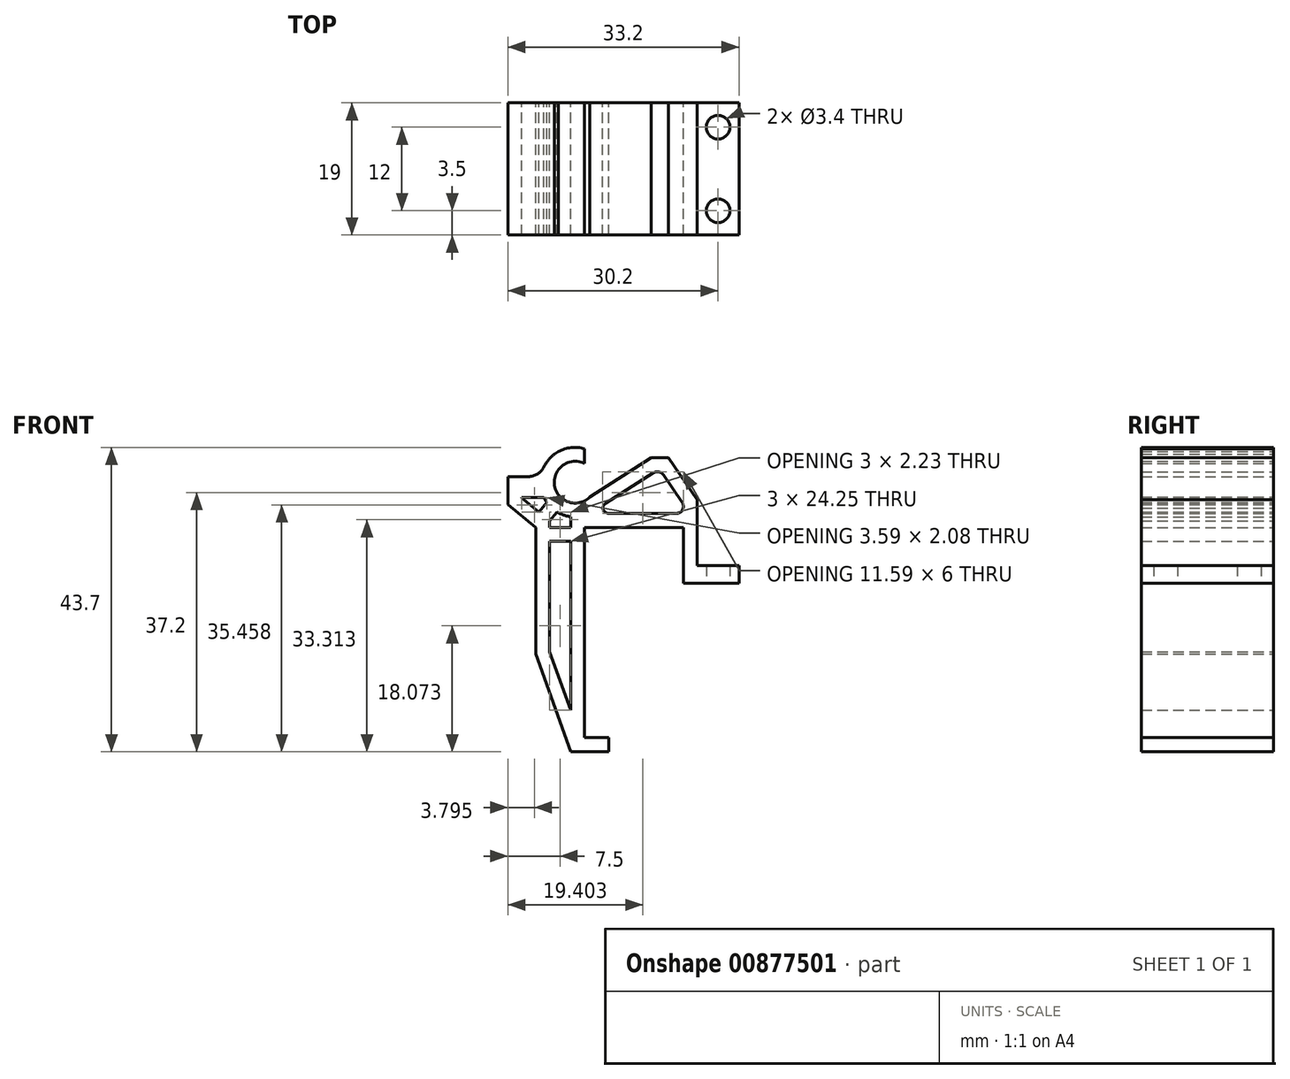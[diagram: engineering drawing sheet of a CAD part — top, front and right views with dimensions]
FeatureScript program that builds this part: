
annotation { "Feature Type Name" : "Feature", "Feature Type Description" : "" }
export const myFeature = defineFeature(function(context is Context, id is Id, definition is map)
    precondition{}
    {
        {
            var Q0;
            Q0=qCreatedBy(makeId("Front.planeOp"),FACE);
            var sketch = newSketch(context, id + "F0", { "sketchPlane" : qUnion([Q0])});
            skLineSegment(sketch, "E0", {"start": v(0, 0) * mm, "end": v(-5.5, 0) * mm});
            skLineSegment(sketch, "E1", {"start": v(0, 0) * mm, "end": v(0, 2) * mm});
            skLineSegment(sketch, "E2", {"start": v(0, 2) * mm, "end": v(-3.5, 2) * mm});
            skLineSegment(sketch, "E3", {"start": v(-3.5, 2) * mm, "end": v(-3.5, 32.2) * mm});
            skLineSegment(sketch, "E4", {"start": v(-3.5, 32.2) * mm, "end": v(10.7, 32.2) * mm});
            skLineSegment(sketch, "E5", {"start": v(10.7, 32.2) * mm, "end": v(10.7, 24.2) * mm});
            skLineSegment(sketch, "E6", {"start": v(10.7, 24.2) * mm, "end": v(18.7, 24.2) * mm});
            skLineSegment(sketch, "E7", {"start": v(18.7, 24.2) * mm, "end": v(18.7, 26.7) * mm});
            skLineSegment(sketch, "E8", {"start": v(18.7, 26.7) * mm, "end": v(12.7, 26.7) * mm});
            skLineSegment(sketch, "E9", {"start": v(12.7, 26.7) * mm, "end": v(12.7, 36.2) * mm});
            skLineSegment(sketch, "E10.0", {"start": v(-0.91, 34.2) * mm, "end": v(10.7, 34.2) * mm});
            skLineSegment(sketch, "E11.0", {"start": v(-10.5, 14) * mm, "end": v(-10.5, 32.2) * mm});
            skLineSegment(sketch, "E12", {"start": v(-10.5, 14) * mm, "end": v(-5.5, 0) * mm});
            skLineSegment(sketch, "E13.0", {"start": v(-8.5, 14.35) * mm, "end": v(-5.5, 5.95) * mm});
            skLineSegment(sketch, "E14.trimOffspring", {"start": v(-8.5, 14.35) * mm, "end": v(-8.5, 30.2) * mm});
            skLineSegment(sketch, "E15", {"start": v(-8.5, 32.2) * mm, "end": v(-5.5, 32.2) * mm});
            skLineSegment(sketch, "E16", {"start": v(-5.5, 30.2) * mm, "end": v(-5.5, 5.95) * mm});
            skLineSegment(sketch, "E17", {"start": v(-3.5, 32.2) * mm, "end": v(6, 32.2) * mm});
            skLineSegment(sketch, "E18", {"start": v(12.7, 36.2) * mm, "end": v(8.59, 42.2) * mm});
            skLineSegment(sketch, "E19.0", {"start": v(10.7, 35.58) * mm, "end": v(7.53, 40.2) * mm});
            skLineSegment(sketch, "E20", {"start": v(11.52, 34.2) * mm, "end": v(11.52, 34.39) * mm});
            skLineSegment(sketch, "E21", {"start": v(-5.5, 0) * mm, "end": v(-5.5, 30.2) * mm});
            skLineSegment(sketch, "E22.0", {"start": v(-14.5, 14) * mm, "end": v(-14.5, 35.5) * mm});
            skLineSegment(sketch, "E23", {"start": v(-10.5, 32.2) * mm, "end": v(-14.5, 35.5) * mm});
            skLineSegment(sketch, "E24", {"start": v(-14.5, 35.5) * mm, "end": v(-14.5, 39.5) * mm});
            skLineSegment(sketch, "E25", {"start": v(-14.5, 39.5) * mm, "end": v(-11.58, 39.5) * mm});
            skLineSegment(sketch, "E26.0", {"start": v(-19.5, 35.5) * mm, "end": v(-19.5, 39.5) * mm});
            skLineSegment(sketch, "E27.0", {"start": v(-12.5, 36.44) * mm, "end": v(-12.5, 36.5) * mm});
            skLineSegment(sketch, "E28", {"start": v(8.59, 42.2) * mm, "end": v(6.09, 42.2) * mm});
            skLineSegment(sketch, "E29.0", {"start": v(7.53, 40.2) * mm, "end": v(6.67, 40.2) * mm});
            skLineSegment(sketch, "E30.trimOffspring", {"start": v(-10.77, 35.02) * mm, "end": v(-12.5, 36.44) * mm});
            skLineSegment(sketch, "E31.trimOffspring", {"start": v(-8.5, 32.2) * mm, "end": v(-8.5, 33.14) * mm});
            skLineSegment(sketch, "E32.trimOffspring", {"start": v(-5.5, 32.2) * mm, "end": v(-5.5, 33.74) * mm});
            skLineSegment(sketch, "E33", {"start": v(-13.88, 0) * mm, "end": v(-4.33, 0) * mm});
            skLineSegment(sketch, "E34.0", {"start": v(-12.5, 36.5) * mm, "end": v(-9.34, 36.5) * mm});
            skLineSegment(sketch, "E35", {"start": v(6.09, 42.2) * mm, "end": v(-2.85, 36.5) * mm});
            skLineSegment(sketch, "E36.0", {"start": v(6.67, 40.2) * mm, "end": v(-0.91, 35.36) * mm});
            skLineSegment(sketch, "E37", {"start": v(-0.91, 34.2) * mm, "end": v(-0.91, 35.36) * mm});
            skArc(sketch, "E38", {"start": v(-6.66, 41.09) * mm, "mid": v(-7.1, 36.73) * mm, "end": v(-2.73, 36.58) * mm});
            skPoint(sketch, "E39.orphan", {"position": v(-10.5, 39.5) * mm});
            skArc(sketch, "E40.0", {"start": v(-9.67, 40.02) * mm, "mid": v(-9.73, 39.75) * mm, "end": v(-9.78, 39.49) * mm});
            skArc(sketch, "E41.trimOffspring", {"start": v(-9.34, 36.5) * mm, "mid": v(-5.68, 33.77) * mm, "end": v(-1.33, 35.15) * mm});
            skPoint(sketch, "E42.orphan", {"position": v(-6.89, 36.5) * mm});
            skLineSegment(sketch, "E43.trimOffspring", {"start": v(-2.9, 36.42) * mm, "end": v(-2.85, 36.5) * mm});
            skLineSegment(sketch, "E44", {"start": v(-0.91, 35.36) * mm, "end": v(-1.33, 35.15) * mm});
            skLineSegment(sketch, "E45", {"start": v(-8.5, 33.14) * mm, "end": v(-7.44, 34.43) * mm});
            skLineSegment(sketch, "E46", {"start": v(-10.04, 34.42) * mm, "end": v(-8.91, 35.79) * mm});
            skPoint(sketch, "E47.orphan", {"position": v(-8.32, 36.5) * mm});
            skPoint(sketch, "E48.orphan", {"position": v(-6.95, 35.02) * mm});
            skLineSegment(sketch, "E49", {"start": v(-10.04, 34.42) * mm, "end": v(-10.77, 35.02) * mm});
            skLineSegment(sketch, "E50.trimOffspring", {"start": v(6, 42.14) * mm, "end": v(6, 42.44) * mm});
            skArc(sketch, "E51.0", {"start": v(-7.8, 42.73) * mm, "mid": v(-8.68, 41.9) * mm, "end": v(-9.34, 40.9) * mm});
            skLineSegment(sketch, "E51.1", {"start": v(-7.26, 43.08) * mm, "end": v(-7.8, 42.73) * mm});
            skLineSegment(sketch, "E52", {"start": v(10.7, 34.2) * mm, "end": v(10.7, 35.58) * mm});
            skArc(sketch, "E53.filletArc", {"start": v(-11.58, 39.5) * mm, "mid": v(-10.26, 39.88) * mm, "end": v(-9.34, 40.9) * mm});
            skArc(sketch, "E54", {"start": v(-3.5, 41.38) * mm, "mid": v(-7.8, 38.22) * mm, "end": v(-2.73, 36.58) * mm});
            skArc(sketch, "E55", {"start": v(-3.5, 43.52) * mm, "mid": v(-9.69, 37.44) * mm, "end": v(-1.33, 35.15) * mm});
            skLineSegment(sketch, "E56.trimOffspring", {"start": v(-6.24, 41.35) * mm, "end": v(-6.66, 41.09) * mm});
            skLineSegment(sketch, "E57.trimOffspring", {"start": v(-3.5, 41.38) * mm, "end": v(-3.5, 43.52) * mm});
            skLineSegment(sketch, "E58", {"start": v(-8.5, 30.2) * mm, "end": v(-8.5, 32.2) * mm});
            skLineSegment(sketch, "E59", {"start": v(-5.5, 30.2) * mm, "end": v(-5.5, 32.39) * mm});
            skLineSegment(sketch, "E60", {"start": v(-8.5, 33.14) * mm, "end": v(-10.04, 34.42) * mm});
            skLineSegment(sketch, "E61", {"start": v(-8.5, 30.2) * mm, "end": v(-5.5, 30.2) * mm});
            skSolve(sketch);
        }
        {
            var Q0;
            {var subQ0=sQuery(id+"F0.wireOp",EDGE,"E15");Q0=makeQuery(id+"F0.imprint","IMPRINT",FACE,{"disambiguationData":[TD([[makeQuery(id+"F0.imprint","IMPRINT",EDGE,{"derivedFrom":subQ0}),-1.0]])]});}
            var Q1;
            {var subQ0=sQuery(id+"F0.wireOp",EDGE,"E45");Q1=makeQuery(id+"F0.imprint","IMPRINT",FACE,{"disambiguationData":[TD([[makeQuery(id+"F0.imprint","IMPRINT",EDGE,{"derivedFrom":subQ0}),1.0]])]});}
            var Q2;
            Q2=makeQuery(id+"F0.imprint","IMPRINT",FACE,{"disambiguationData":[TD([[makeQuery(id+"F0.imprint","IMPRINT",EDGE,{"derivedFrom":sQuery(id+"F0.wireOp",EDGE,"E11.0")}),-1.0]])]});
            var Q3;
            {var subQ15=sQuery(id+"F0.wireOp",EDGE,"E0");Q3=makeQuery(id+"F0.imprint","IMPRINT",FACE,{"disambiguationData":[TD([[makeQuery(id+"F0.imprint","IMPRINT",EDGE,{"derivedFrom":subQ15}),-1.0]])]});}
            extrude(context, id + "F1", {"entities" : qUnion([Q0, Q1, Q2, Q3]), "depth" : 19 * mm, "offsetDistance" : 25 * mm});
        }
        {
            var Q0;
            Q0=makeQuery(id+"F1.opExtrude","SWEPT_FACE",FACE,{"disambiguationData":[OSD([sQuery(id+"F0.wireOp",EDGE,"E8")])]});
            var sketch = newSketch(context, id + "F2", { "sketchPlane" : qUnion([Q0])});
            skLineSegment(sketch, "E62", {"start": v(15.7, -19) * mm, "end": v(15.7, 0) * mm});
            skLineSegment(sketch, "E63", {"start": v(15.7, -9.5) * mm, "end": v(15.7, -15.5) * mm});
            skLineSegment(sketch, "E64", {"start": v(15.7, -15.5) * mm, "end": v(15.7, -3.5) * mm});
            skSolve(sketch);
        }
        {
            var Q0;
            Q0=sQuery(id+"F2.wireOp",VERTEX,"E63.end");
            var Q1;
            Q1=sQuery(id+"F2.wireOp",VERTEX,"E64.end");
            var Q2;
            Q2=makeQuery(id+"F1.opExtrude","SWEPT_BODY",BODY,{"disambiguationData":[OSD([sQuery(id+"F0.wireOp",EDGE,"E0"),sQuery(id+"F0.wireOp",EDGE,"E1"),sQuery(id+"F0.wireOp",EDGE,"E2"),sQuery(id+"F0.wireOp",EDGE,"E3"),sQuery(id+"F0.wireOp",EDGE,"E4"),sQuery(id+"F0.wireOp",EDGE,"E5"),sQuery(id+"F0.wireOp",EDGE,"E6"),sQuery(id+"F0.wireOp",EDGE,"E7"),sQuery(id+"F0.wireOp",EDGE,"E8"),sQuery(id+"F0.wireOp",EDGE,"E9"),sQuery(id+"F0.wireOp",EDGE,"E10.0"),sQuery(id+"F0.wireOp",EDGE,"E11.0"),sQuery(id+"F0.wireOp",EDGE,"E12"),sQuery(id+"F0.wireOp",EDGE,"E13.0"),sQuery(id+"F0.wireOp",EDGE,"E14.trimOffspring"),sQuery(id+"F0.wireOp",EDGE,"E17"),sQuery(id+"F0.wireOp",EDGE,"E18"),sQuery(id+"F0.wireOp",EDGE,"E19.0"),sQuery(id+"F0.wireOp",EDGE,"E21"),sQuery(id+"F0.wireOp",EDGE,"E23"),sQuery(id+"F0.wireOp",EDGE,"E24"),sQuery(id+"F0.wireOp",EDGE,"E25"),sQuery(id+"F0.wireOp",EDGE,"E27.0"),sQuery(id+"F0.wireOp",EDGE,"E28"),sQuery(id+"F0.wireOp",EDGE,"E29.0"),sQuery(id+"F0.wireOp",EDGE,"E30.trimOffspring"),sQuery(id+"F0.wireOp",EDGE,"E33"),sQuery(id+"F0.wireOp",EDGE,"E34.0"),sQuery(id+"F0.wireOp",EDGE,"E35"),sQuery(id+"F0.wireOp",EDGE,"E36.0"),sQuery(id+"F0.wireOp",EDGE,"E37"),sQuery(id+"F0.wireOp",EDGE,"E38"),sQuery(id+"F0.wireOp",EDGE,"E41.trimOffspring"),sQuery(id+"F0.wireOp",EDGE,"E45"),sQuery(id+"F0.wireOp",EDGE,"xdzNrTBE-XzyX-zclI-OnCp-i4VAQ6aGnxey"),sQuery(id+"F0.wireOp",EDGE,"E49"),sQuery(id+"F0.wireOp",EDGE,"7aTHKKxO-Tvbm-gAxb-JWcQ-REEeTTHWHdVK"),sQuery(id+"F0.wireOp",EDGE,"faeb26e9-fd7f-4cee-b89a-338b25216712.0"),sQuery(id+"F0.wireOp",EDGE,"E51.0"),sQuery(id+"F0.wireOp",EDGE,"E51.1"),sQuery(id+"F0.wireOp",EDGE,"t1PeDV6i-6xjs-lc1O-n51G-zDklkPdjoq5l"),sQuery(id+"F0.wireOp",EDGE,"E52"),sQuery(id+"F0.wireOp",EDGE,"E53.filletArc")])]});
            hole(context, id + "F3", {"style" : HoleStyle.SIMPLE, "endStyle" : HoleEndStyle.THROUGH, "standardTappedOrClearance" : lookupTablePath({ "fit" : "Normal", "standard" : "ISO", "size" : "M3", "type" : "Clearance" }), "standardBlindInLast" : lookupTablePath({ "fit" : "Normal", "standard" : "ISO", "size" : "M3", "type" : "Clearance" }), "holeDiameter" : 3.4 * mm, "majorDiameter" : 5 * mm, "isTappedThrough" : true, "tappedDepth" : 12 * mm, "tapClearance" : 3, "locations" : qUnion([Q0, Q1]), "scope" : qUnion([Q2]), "startStyle" : HoleStartStyle.PART});
        }
        {
            var Q0;
            Q0=makeQuery(id+"F1.opExtrude","SWEPT_EDGE",EDGE,{"disambiguationData":[OSD([sQuery(id+"F0.wireOp",EDGE,"E19.0"),sQuery(id+"F0.wireOp",EDGE,"E52")])]});
            var Q1;
            Q1=makeQuery(id+"F1.opExtrude","SWEPT_EDGE",EDGE,{"disambiguationData":[OSD([sQuery(id+"F0.wireOp",EDGE,"E19.0"),sQuery(id+"F0.wireOp",EDGE,"E29.0")])]});
            var Q2;
            Q2=makeQuery(id+"F1.opExtrude","SWEPT_EDGE",EDGE,{"disambiguationData":[OSD([sQuery(id+"F0.wireOp",EDGE,"E29.0"),sQuery(id+"F0.wireOp",EDGE,"E36.0")])]});
            var Q3;
            Q3=makeQuery(id+"F1.opExtrude","SWEPT_EDGE",EDGE,{"disambiguationData":[OSD([sQuery(id+"F0.wireOp",EDGE,"E36.0"),sQuery(id+"F0.wireOp",EDGE,"E37")])]});
            var Q4;
            Q4=makeQuery(id+"F1.opExtrude","SWEPT_EDGE",EDGE,{"disambiguationData":[OSD([sQuery(id+"F0.wireOp",EDGE,"E10.0"),sQuery(id+"F0.wireOp",EDGE,"E37")])]});
            var Q5;
            Q5=makeQuery(id+"F1.opExtrude","SWEPT_EDGE",EDGE,{"disambiguationData":[OSD([sQuery(id+"F0.wireOp",EDGE,"E10.0"),sQuery(id+"F0.wireOp",EDGE,"E52")])]});
            fillet(context, id + "F4", {"entities" : qUnion([Q0, Q1, Q2, Q3, Q4, Q5]), "radius" : 1 * mm, "tangentPropagation" : true, "allowEdgeOverflow" : false});
        }
    });
